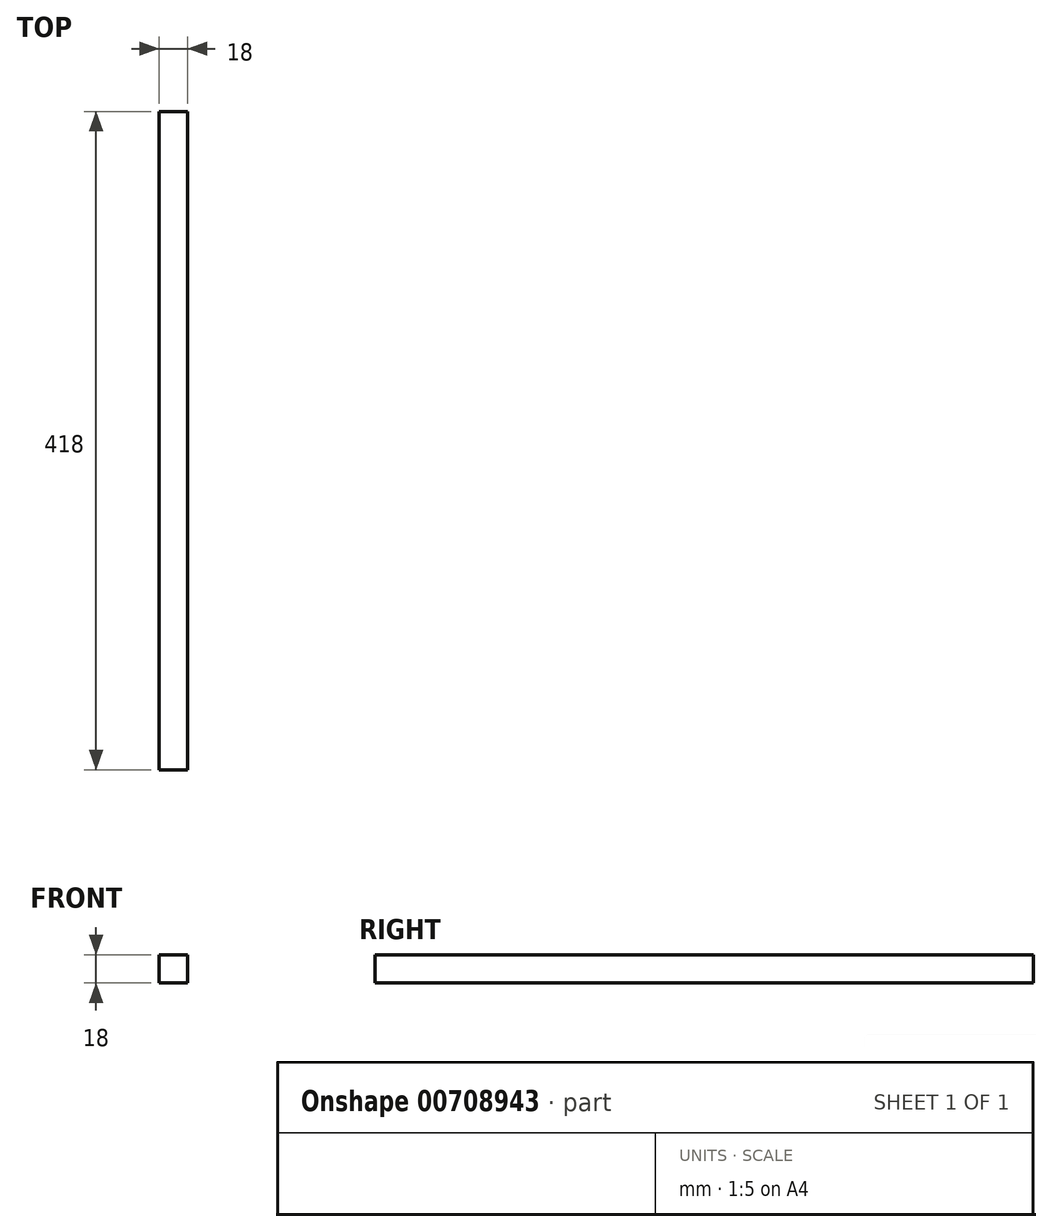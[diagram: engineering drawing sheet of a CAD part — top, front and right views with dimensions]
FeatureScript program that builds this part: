
annotation { "Feature Type Name" : "Feature", "Feature Type Description" : "" }
export const myFeature = defineFeature(function(context is Context, id is Id, definition is map)
    precondition{}
    {
        {
            var Q0;
            Q0=qCreatedBy(makeId("Right.planeOp"),FACE);
            var sketch = newSketch(context, id + "F0", { "sketchPlane" : qUnion([Q0])});
            skLineSegment(sketch, "E0.bottom", {"start": v(0, 0) * mm, "end": v(348, 0) * mm});
            skLineSegment(sketch, "E0.top", {"start": v(-70, 810) * mm, "end": v(348, 810) * mm});
            skLineSegment(sketch, "E0.left", {"start": v(0, 0) * mm, "end": v(0, 380) * mm});
            skLineSegment(sketch, "E0.right", {"start": v(348, 0) * mm, "end": v(348, 810) * mm});
            skLineSegment(sketch, "E1.top", {"start": v(0, 380) * mm, "end": v(-70, 380) * mm});
            skLineSegment(sketch, "E1.right", {"start": v(-70, 810) * mm, "end": v(-70, 380) * mm});
            skPoint(sketch, "E2.orphan", {"position": v(0, 810) * mm});
            skSolve(sketch);
        }
        {
            var Q0;
            Q0=makeQuery(id+"F0.imprint","IMPRINT",FACE,{"disambiguationData":[TD([[makeQuery(id+"F0.imprint","IMPRINT",EDGE,{"derivedFrom":sQuery(id+"F0.wireOp",EDGE,"E0.bottom")}),1.0]])]});
            extrude(context, id + "F1", {"entities" : qUnion([Q0]), "depth" : 18 * mm, "offsetDistance" : 25 * mm});
        }
        {
            var Q0;
            Q0=makeQuery(id+"F1.opExtrude","SWEPT_EDGE",EDGE,{"disambiguationData":[OSD([sQuery(id+"F0.wireOp",EDGE,"E0.top"),sQuery(id+"F0.wireOp",EDGE,"E1.right")])]});
            var Q1;
            Q1=makeQuery(id+"F1.opExtrude","SWEPT_EDGE",EDGE,{"disambiguationData":[OSD([sQuery(id+"F0.wireOp",EDGE,"E0.top"),sQuery(id+"F0.wireOp",EDGE,"E0.right")])]});
            fillet(context, id + "F2", {"entities" : qUnion([Q0, Q1]), "radius" : 100 * mm, "tangentPropagation" : true, "allowEdgeOverflow" : false});
        }
        {
            var Q0;
            Q0=makeQuery(id+"F1.opExtrude","SWEPT_EDGE",EDGE,{"disambiguationData":[OSD([sQuery(id+"F0.wireOp",EDGE,"E1.top"),sQuery(id+"F0.wireOp",EDGE,"E1.right")])]});
            fillet(context, id + "F3", {"entities" : qUnion([Q0]), "radius" : 6 * mm, "tangentPropagation" : true, "allowEdgeOverflow" : false});
        }
        {
            var Q0;
            Q0=makeQuery(id+"F1.opExtrude","SWEPT_BODY",BODY,{"disambiguationData":[OSD([sQuery(id+"F0.wireOp",EDGE,"E0.bottom"),sQuery(id+"F0.wireOp",EDGE,"E0.top"),sQuery(id+"F0.wireOp",EDGE,"E0.left"),sQuery(id+"F0.wireOp",EDGE,"E0.right"),sQuery(id+"F0.wireOp",EDGE,"E1.top"),sQuery(id+"F0.wireOp",EDGE,"E1.right")])]});
            transform(context, id + "F4", {"entities" : qUnion([Q0]), "transformType" : TransformType.TRANSLATION_3D, "dx" : 0 * mm, "dy" : 0 * mm, "dz" : 0 * mm, "makeCopy" : true});
        }
        {
            var Q0;
            Q0=makeQuery(id+"F1.opExtrude","SWEPT_FACE",FACE,{"disambiguationData":[OSD([sQuery(id+"F0.wireOp",EDGE,"E0.top")])]});
            var sketch = newSketch(context, id + "F5", { "sketchPlane" : qUnion([Q0])});
            skLineSegment(sketch, "E3.bottom", {"start": v(0, 348) * mm, "end": v(18, 348) * mm});
            skLineSegment(sketch, "E3.top", {"start": v(0, -70) * mm, "end": v(18, -70) * mm});
            skLineSegment(sketch, "E3.left", {"start": v(0, 348) * mm, "end": v(0, -70) * mm});
            skLineSegment(sketch, "E3.right", {"start": v(18, 348) * mm, "end": v(18, -70) * mm});
            skSolve(sketch);
        }
        {
            var Q0;
            Q0 = qSketchRegion(id + "F5", true);
            extrude(context, id + "F6", {"entities" : qUnion([Q0]), "operationType" : NewBodyOperationType.REMOVE, "oppositeDirection" : true, "depth" : (300 - 58) * mm, "offsetDistance" : 25 * mm});
        }
        {
            var Q0;
            Q0=makeQuery(id+"F4.opPattern","COPY",FACE,{"derivedFrom":makeQuery(id+"F1.opExtrude","SWEPT_FACE",FACE,{"disambiguationData":[OSD([sQuery(id+"F0.wireOp",EDGE,"E0.bottom")])]}),"instanceName":"1"});
            var sketch = newSketch(context, id + "F7", { "sketchPlane" : qUnion([Q0])});
            skLineSegment(sketch, "E4.bottom", {"start": v(0, -348) * mm, "end": v(18, -348) * mm});
            skLineSegment(sketch, "E4.top", {"start": v(0, 70) * mm, "end": v(18, 70) * mm});
            skLineSegment(sketch, "E4.left", {"start": v(0, -348) * mm, "end": v(0, 70) * mm});
            skLineSegment(sketch, "E4.right", {"start": v(18, -348) * mm, "end": v(18, 70) * mm});
            skSolve(sketch);
        }
        {
            var Q0;
            {var subQ0=sQuery(id+"F7.wireOp",EDGE,"E4.top");Q0=makeQuery(id+"F7.imprint","IMPRINT",FACE,{"disambiguationData":[TD([[makeQuery(id+"F7.imprint","IMPRINT",EDGE,{"derivedFrom":subQ0}),-1.0]])]});}
            var Q1;
            {var subQ0=sQuery(id+"F0.wireOp",EDGE,"E0.bottom");var subQ1=makeQuery(id+"F4.opPattern","COPY",EDGE,{"derivedFrom":makeQuery(id+"F1.opExtrude","SWEPT_EDGE",EDGE,{"disambiguationData":[OSD([subQ0,sQuery(id+"F0.wireOp",EDGE,"E0.left")])]}),"instanceName":"1"});Q1=makeQuery(id+"F7.imprint","IMPRINT",FACE,{"disambiguationData":[TD([[makeQuery(id+"F7.imprint","IMPRINT",EDGE,{"derivedFrom":subQ1}),1.0]])]});}
            extrude(context, id + "F8", {"entities" : qUnion([Q0, Q1]), "operationType" : NewBodyOperationType.REMOVE, "oppositeDirection" : true, "depth" : 550 * mm, "offsetDistance" : 25 * mm});
        }
    });
